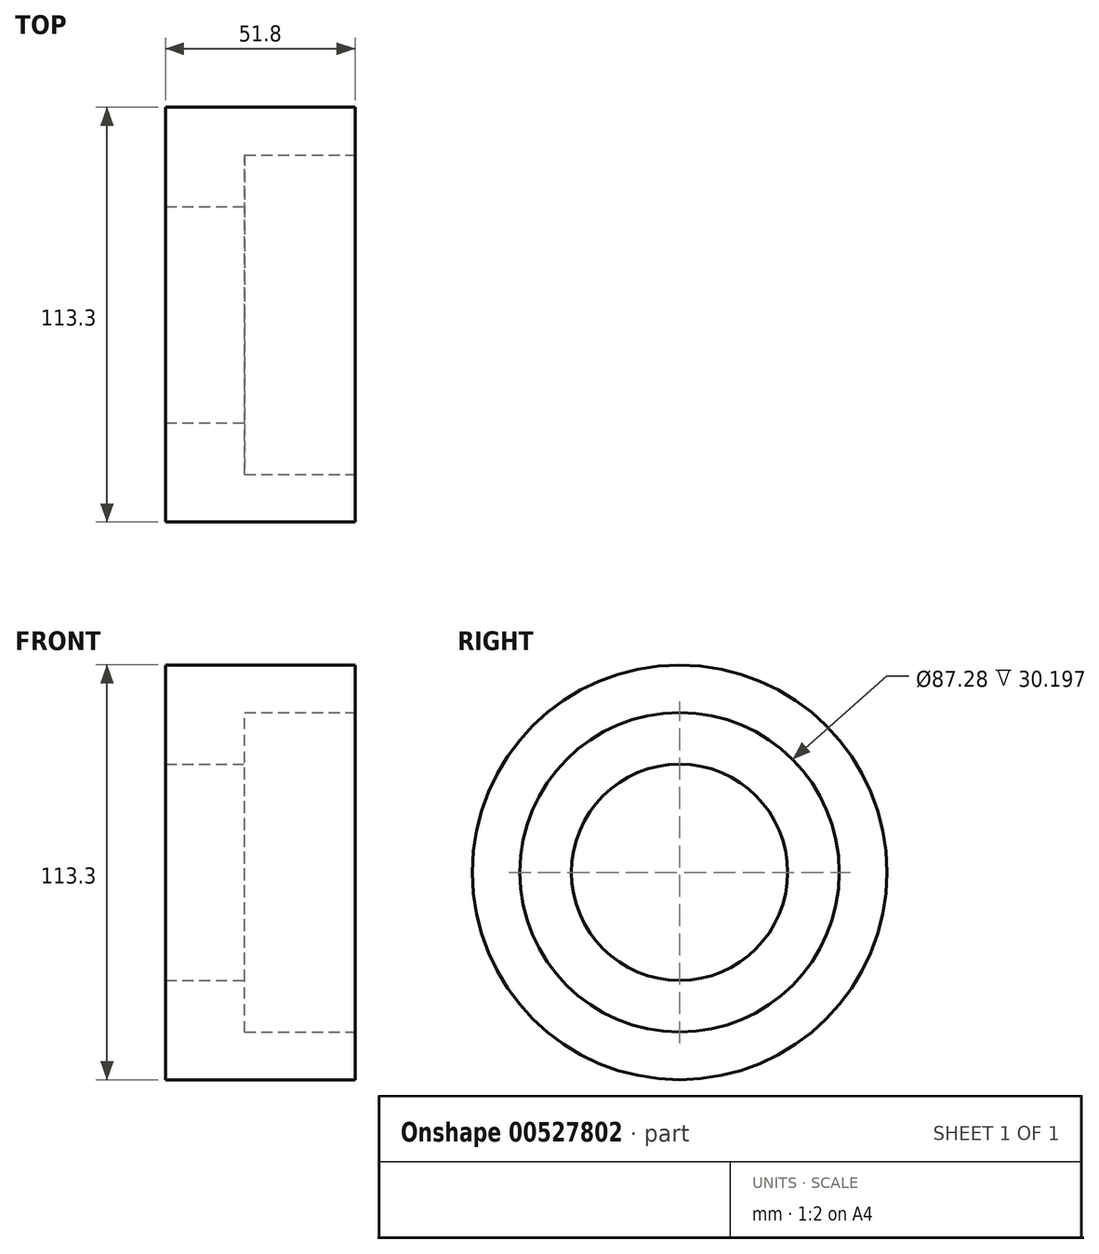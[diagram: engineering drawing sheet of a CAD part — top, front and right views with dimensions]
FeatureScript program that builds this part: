
annotation { "Feature Type Name" : "Feature", "Feature Type Description" : "" }
export const myFeature = defineFeature(function(context is Context, id is Id, definition is map)
    precondition{}
    {
        {
            var Q0;
            Q0=qCreatedBy(makeId("Front.planeOp"),FACE);
            var sketch = newSketch(context, id + "F0", { "sketchPlane" : qUnion([Q0])});
            skLineSegment(sketch, "E0.top", {"start": v(-31.08, 29.54) * mm, "end": v(-9.48, 29.54) * mm});
            skLineSegment(sketch, "E0.left", {"start": v(-31.08, 43.64) * mm, "end": v(-31.08, 29.54) * mm});
            skLineSegment(sketch, "E0.right", {"start": v(-9.48, 43.64) * mm, "end": v(-9.48, 29.54) * mm});
            skLineSegment(sketch, "E1.right", {"start": v(-9.48, 29.54) * mm, "end": v(-9.48, 43.64) * mm});
            skLineSegment(sketch, "E2.top", {"start": v(-31.08, 56.65) * mm, "end": v(20.72, 56.65) * mm});
            skLineSegment(sketch, "E2.left", {"start": v(-31.08, 43.64) * mm, "end": v(-31.08, 56.65) * mm});
            skLineSegment(sketch, "E2.right", {"start": v(20.72, 43.64) * mm, "end": v(20.72, 56.65) * mm});
            skLineSegment(sketch, "E3", {"start": v(-9.48, 43.64) * mm, "end": v(20.72, 43.64) * mm});
            skLineSegment(sketch, "E4", {"start": v(0, 0) * mm, "end": v(-113.73, 0) * mm});
            skSolve(sketch);
        }
        {
            var Q0;
            Q0 = qSketchRegion(id + "F0", true);
            var Q1;
            Q1=makeQuery(id+"F0.imprint","IMPRINT",FACE,{"disambiguationData":[TD([[makeQuery(id+"F0.imprint","IMPRINT",EDGE,{"derivedFrom":sQuery(id+"F0.wireOp",EDGE,"E0.top")}),1.0]])]});
            var Q2;
            Q2=sQuery(id+"F0.wireOp",EDGE,"E4");
            revolve(context, id + "F1", {"entities" : qUnion([Q0, Q1]), "axis" : qUnion([Q2]), "revolveType" : RevolveType.FULL});
        }
    });
